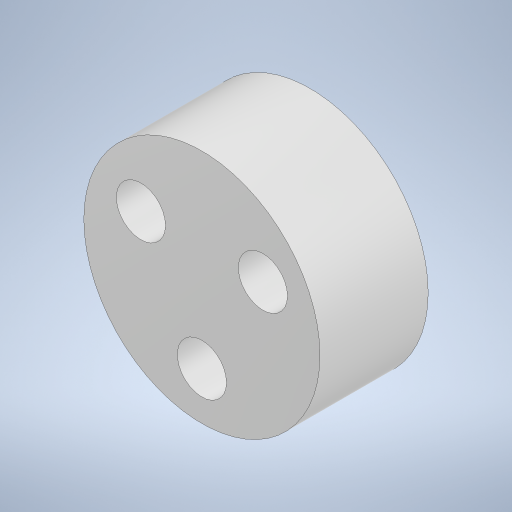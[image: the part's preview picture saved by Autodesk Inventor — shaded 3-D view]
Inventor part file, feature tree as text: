
AUTODESK INVENTOR PART (.ipt)
format: ipt  version: 2023.1 (Build 271208000, 208)  size: 230,400 bytes
history: native  units: mm
features: other x3, sketch x1
ambient origin geometry x8: Origin, YZ Plane, XZ Plane, XY Plane, X Axis, Y Axis, Z Axis, Center Point
bodies: Solid1 (feature_tree)
feature tree (4):
  other  "カム3.ipt"
  other  "Solid1::カム3.ipt"
  other  "TaggingFeature1"
  sketch  "Sketch1"  dims[d0=10.0mm]
